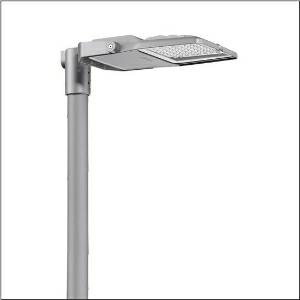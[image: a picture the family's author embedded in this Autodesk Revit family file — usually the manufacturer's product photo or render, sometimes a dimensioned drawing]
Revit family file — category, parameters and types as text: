
# Revit family: floodlight_fl_21_mini___pl61_5xa7775c2c3a_8aba
name_source: partatom
category: Lighting Fixtures
units: mm (PartAtom-declared; Revit-internal decimal feet)

## family parameters
Cut with Voids When Loaded = No
Host = Face
Light Source = No
Part Type = Normal
Room Calculation Point = No
Round Connector Dimension = Use Diameter
Shared = No

## types (1)
- --- (1 x LED, 11960 lm, 89 W, 3000K)
    Apparent Load = 89 VA
    CIE Flux Codes = 33 65 98 100 100
    Color Rendering = 70
    Color Temperature = 3000K
    Default Elevation = 1800 mm
    Description = Floodlight FL 21 mini, floodlight, primary light control with lens, of PMMA, primary optical cover: protective disc, of toughened safety glass, transparent, light distribution: PL61, light emission: direct distribution, installation type: surface-mounted, LED, High Power LED, rated luminous flux: 11.960lm, luminous efficacy: 134lm/W, light colour: 730, colour temperature: 3000K, control gear: Smart Interface (Zhaga), control: flexible luminous flux parameterisation, time-dependent luminous flux control, constant luminous flux control, overheat protection, pre-setting: logarithmic dimming characteristic, with terminal, 6-pole, mains connection: 220..240V, AC, 50/60Hz, start of lifetime: 89W, end of service life: 94W, reduction: 43W, luminaire housing, of diecast aluminium, powder-coated, Siteco® metallic grey (DB 702S), corrosivity category C5 mid according to DIN EN ISO 12944, suitable for swimming pools, chlorine-resistant, sealing non-destructively replaceable, please order mast flange separately, mast bracket, of steel, galvanised, powder-coated, Siteco® metallic grey (DB 702S), Smart Interface above, protection rating (complete): IP66, insulation class (complete): insulation class II (safety insulation), certification: CE, ENEC, VDE, protection symbol: D, impact resistance: IK08, permissible operating ambient temperature: -40..+40°C, permissible operating ambient temperature for outdoor applications: -40..+50°C, standard: DIN EN 12944, LABS conformity tested according to VDMA 24364:2018-05, packaging unit: 1 piece

Light Distribution: PL61
    Height = 70 mm
    Lamp = 1 x LED
    Lamp Light Flux = 11960 lm
    Lamp Power = 89 W
    Lamp count = 1
    Length = 485 mm
    Luminous efficacy = 134 lm/W
    Manufacturer = Siteco
    ModVariant = No
    Model = 5XA7775C2C3A
    Number of Poles = 1
    OnlyDefault = Yes
    Power Factor = 1
    Product Name = Floodlight FL 21 mini | PL61
    Product group = floodlight | pylon annexe
    ProductGroupID = 6201
    Protection Class = Protection class II
    Protection Degree = IP 66
    RLX_Detail_Level = 1
    RLX_Emergency_Light_Flux = 0 lm
    RLX_Emergency_Type = 0
    RLX_Emergency_Type_DB = No
    RlxData = <blob elided: 101157 chars, md5=86be0dd1>
    Socket = socket
    Standby Power = 0 W
    System Light Flux = 11960 lm
    System Power = 89 W
    Type Comments = factory setting: luminous flux: 100 % | dim-lin: 254 | 456 mA
    Type Image = l_1007125.jpg
    URL = http://relux.com
    VarID = @adj_193531
    Voltage = 0 V
    Weight = 0.00 kg
    Width = 337 mm

## geometry (parser evidence)
native form markers: Blend x4, Sweep x12
no freeform markers — native parametric forms only
